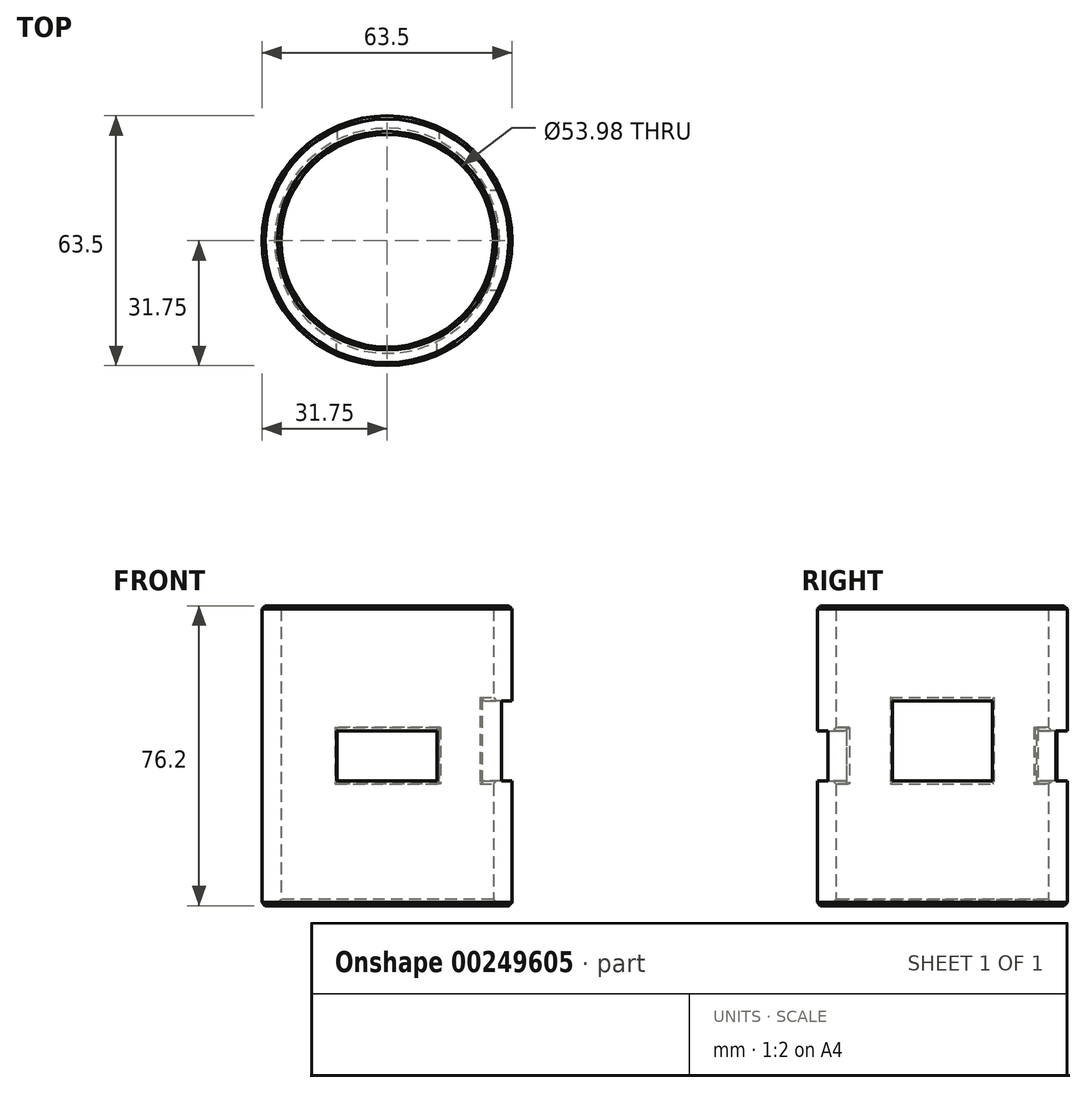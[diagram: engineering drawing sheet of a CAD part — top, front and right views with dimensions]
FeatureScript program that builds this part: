
annotation { "Feature Type Name" : "Feature", "Feature Type Description" : "" }
export const myFeature = defineFeature(function(context is Context, id is Id, definition is map)
    precondition{}
    {
        {
            var Q0;
            Q0=qCreatedBy(makeId("Top.planeOp"),FACE);
            var sketch = newSketch(context, id + "F0", { "sketchPlane" : qUnion([Q0])});
            skCircle(sketch, "E0", {"center": v(0, 0) * mm, "radius": 26.99 * mm});
            skCircle(sketch, "E1", {"center": v(0, 0) * mm, "radius": 31.75 * mm});
            skSolve(sketch);
        }
        {
            var Q0;
            Q0=makeQuery(id+"F0.imprint","IMPRINT",FACE,{"disambiguationData":[TD([[makeQuery(id+"F0.imprint","IMPRINT",EDGE,{"derivedFrom":sQuery(id+"F0.wireOp",EDGE,"E0")}),-1.0]])]});
            extrude(context, id + "F1", {"entities" : qUnion([Q0]), "depth" : 76.2 * mm});
        }
        {
            var Q0;
            Q0=qCreatedBy(makeId("Front.planeOp"),FACE);
            var sketch = newSketch(context, id + "F2", { "sketchPlane" : qUnion([Q0])});
            skLineSegment(sketch, "E2.bottom", {"start": v(13.22, 31.75) * mm, "end": v(-12.7, 31.75) * mm});
            skLineSegment(sketch, "E2.top", {"start": v(13.22, 44.45) * mm, "end": v(-12.7, 44.45) * mm});
            skLineSegment(sketch, "E2.left", {"start": v(13.22, 31.75) * mm, "end": v(13.22, 44.45) * mm});
            skLineSegment(sketch, "E2.right", {"start": v(-12.7, 31.75) * mm, "end": v(-12.7, 44.45) * mm});
            skSolve(sketch);
        }
        {
            var Q0;
            Q0 = qSketchRegion(id + "F2", true);
            extrude(context, id + "F3", {"entities" : qUnion([Q0]), "operationType" : NewBodyOperationType.REMOVE, "oppositeDirection" : true, "depth" : 76.2 * mm});
        }
        {
            var Q0;
            Q0=qCreatedBy(makeId("Front.planeOp"),FACE);
            var sketch = newSketch(context, id + "F4", { "sketchPlane" : qUnion([Q0])});
            skLineSegment(sketch, "E3.bottom", {"start": v(-12.77, 31.75) * mm, "end": v(12.7, 31.75) * mm});
            skLineSegment(sketch, "E3.top", {"start": v(-12.77, 44.45) * mm, "end": v(12.7, 44.45) * mm});
            skLineSegment(sketch, "E3.left", {"start": v(-12.77, 31.75) * mm, "end": v(-12.77, 44.45) * mm});
            skLineSegment(sketch, "E3.right", {"start": v(12.7, 31.75) * mm, "end": v(12.7, 44.45) * mm});
            skSolve(sketch);
        }
        {
            var Q0;
            Q0=makeQuery(id+"F4.imprint","IMPRINT",FACE,{"disambiguationData":[TD([[makeQuery(id+"F4.imprint","IMPRINT",EDGE,{"derivedFrom":sQuery(id+"F4.wireOp",EDGE,"E3.bottom")}),1.0]])]});
            extrude(context, id + "F5", {"entities" : qUnion([Q0]), "operationType" : NewBodyOperationType.REMOVE, "depth" : 76.2 * mm});
        }
        {
            var Q0;
            Q0=qCreatedBy(makeId("Right.planeOp"),FACE);
            var sketch = newSketch(context, id + "F6", { "sketchPlane" : qUnion([Q0])});
            skLineSegment(sketch, "E4.bottom", {"start": v(-12.7, 31.75) * mm, "end": v(12.7, 31.75) * mm});
            skLineSegment(sketch, "E4.top", {"start": v(-12.7, 52.07) * mm, "end": v(12.7, 52.07) * mm});
            skLineSegment(sketch, "E4.left", {"start": v(-12.7, 31.75) * mm, "end": v(-12.7, 52.07) * mm});
            skLineSegment(sketch, "E4.right", {"start": v(12.7, 31.75) * mm, "end": v(12.7, 52.07) * mm});
            skSolve(sketch);
        }
        {
            var Q0;
            Q0 = qSketchRegion(id + "F6", true);
            extrude(context, id + "F7", {"entities" : qUnion([Q0]), "operationType" : NewBodyOperationType.REMOVE, "depth" : 76.2 * mm});
        }
        {
            var Q0;
            Q0=makeQuery(id+"F7.boolean.opBoolean","INTERSECT",EDGE,{"derivedFrom":[makeQuery(id+"F1.opExtrude","SWEPT_FACE",FACE,{"disambiguationData":[OSD([sQuery(id+"F0.wireOp",EDGE,"E0")])]}),makeQuery(id+"F7.opExtrude","SWEPT_FACE",FACE,{"disambiguationData":[OSD([sQuery(id+"F6.wireOp",EDGE,"E4.bottom")])]})]});
            var Q1;
            Q1=makeQuery(id+"F7.boolean.opBoolean","INTERSECT",EDGE,{"derivedFrom":[makeQuery(id+"F1.opExtrude","SWEPT_FACE",FACE,{"disambiguationData":[OSD([sQuery(id+"F0.wireOp",EDGE,"E0")])]}),makeQuery(id+"F7.opExtrude","SWEPT_FACE",FACE,{"disambiguationData":[OSD([sQuery(id+"F6.wireOp",EDGE,"E4.right")])]})]});
            var Q2;
            Q2=makeQuery(id+"F7.boolean.opBoolean","INTERSECT",EDGE,{"derivedFrom":[makeQuery(id+"F1.opExtrude","SWEPT_FACE",FACE,{"disambiguationData":[OSD([sQuery(id+"F0.wireOp",EDGE,"E0")])]}),makeQuery(id+"F7.opExtrude","SWEPT_FACE",FACE,{"disambiguationData":[OSD([sQuery(id+"F6.wireOp",EDGE,"E4.top")])]})]});
            var Q3;
            Q3=makeQuery(id+"F7.boolean.opBoolean","INTERSECT",EDGE,{"derivedFrom":[makeQuery(id+"F1.opExtrude","SWEPT_FACE",FACE,{"disambiguationData":[OSD([sQuery(id+"F0.wireOp",EDGE,"E0")])]}),makeQuery(id+"F7.opExtrude","SWEPT_FACE",FACE,{"disambiguationData":[OSD([sQuery(id+"F6.wireOp",EDGE,"E4.left")])]})]});
            var Q4;
            Q4=makeQuery(id+"F3.boolean.opBoolean","INTERSECT",EDGE,{"derivedFrom":[makeQuery(id+"F1.opExtrude","SWEPT_FACE",FACE,{"disambiguationData":[OSD([sQuery(id+"F0.wireOp",EDGE,"E0")])]}),makeQuery(id+"F3.opExtrude","SWEPT_FACE",FACE,{"disambiguationData":[OSD([sQuery(id+"F2.wireOp",EDGE,"E2.left")])]})]});
            var Q5;
            Q5=makeQuery(id+"F3.boolean.opBoolean","INTERSECT",EDGE,{"derivedFrom":[makeQuery(id+"F1.opExtrude","SWEPT_FACE",FACE,{"disambiguationData":[OSD([sQuery(id+"F0.wireOp",EDGE,"E0")])]}),makeQuery(id+"F3.opExtrude","SWEPT_FACE",FACE,{"disambiguationData":[OSD([sQuery(id+"F2.wireOp",EDGE,"E2.bottom")])]})]});
            var Q6;
            Q6=makeQuery(id+"F3.boolean.opBoolean","INTERSECT",EDGE,{"derivedFrom":[makeQuery(id+"F1.opExtrude","SWEPT_FACE",FACE,{"disambiguationData":[OSD([sQuery(id+"F0.wireOp",EDGE,"E0")])]}),makeQuery(id+"F3.opExtrude","SWEPT_FACE",FACE,{"disambiguationData":[OSD([sQuery(id+"F2.wireOp",EDGE,"E2.top")])]})]});
            var Q7;
            Q7=makeQuery(id+"F3.boolean.opBoolean","INTERSECT",EDGE,{"derivedFrom":[makeQuery(id+"F1.opExtrude","SWEPT_FACE",FACE,{"disambiguationData":[OSD([sQuery(id+"F0.wireOp",EDGE,"E0")])]}),makeQuery(id+"F3.opExtrude","SWEPT_FACE",FACE,{"disambiguationData":[OSD([sQuery(id+"F2.wireOp",EDGE,"E2.right")])]})]});
            var Q8;
            Q8=makeQuery(id+"F5.boolean.opBoolean","INTERSECT",EDGE,{"derivedFrom":[makeQuery(id+"F1.opExtrude","SWEPT_FACE",FACE,{"disambiguationData":[OSD([sQuery(id+"F0.wireOp",EDGE,"E0")])]}),makeQuery(id+"F5.opExtrude","SWEPT_FACE",FACE,{"disambiguationData":[OSD([sQuery(id+"F4.wireOp",EDGE,"E3.right")])]})]});
            var Q9;
            Q9=makeQuery(id+"F5.boolean.opBoolean","INTERSECT",EDGE,{"derivedFrom":[makeQuery(id+"F1.opExtrude","SWEPT_FACE",FACE,{"disambiguationData":[OSD([sQuery(id+"F0.wireOp",EDGE,"E0")])]}),makeQuery(id+"F5.opExtrude","SWEPT_FACE",FACE,{"disambiguationData":[OSD([sQuery(id+"F4.wireOp",EDGE,"E3.left")])]})]});
            var Q10;
            Q10=makeQuery(id+"F5.boolean.opBoolean","INTERSECT",EDGE,{"derivedFrom":[makeQuery(id+"F1.opExtrude","SWEPT_FACE",FACE,{"disambiguationData":[OSD([sQuery(id+"F0.wireOp",EDGE,"E0")])]}),makeQuery(id+"F5.opExtrude","SWEPT_FACE",FACE,{"disambiguationData":[OSD([sQuery(id+"F4.wireOp",EDGE,"E3.bottom")])]})]});
            var Q11;
            Q11=makeQuery(id+"F5.boolean.opBoolean","INTERSECT",EDGE,{"derivedFrom":[makeQuery(id+"F1.opExtrude","SWEPT_FACE",FACE,{"disambiguationData":[OSD([sQuery(id+"F0.wireOp",EDGE,"E0")])]}),makeQuery(id+"F5.opExtrude","SWEPT_FACE",FACE,{"disambiguationData":[OSD([sQuery(id+"F4.wireOp",EDGE,"E3.top")])]})]});
            chamfer(context, id + "F8", {"entities" : qUnion([Q0, Q1, Q2, Q3, Q4, Q5, Q6, Q7, Q8, Q9, Q10, Q11]), "width" : 0.81 * mm, "tangentPropagation" : true});
        }
        {
            var Q0;
            Q0=makeQuery(id+"F1.opExtrude","CAP_EDGE",EDGE,{"disambiguationData":[OSD([sQuery(id+"F0.wireOp",EDGE,"E0")])],"isStart":false});
            var Q1;
            Q1=makeQuery(id+"F1.opExtrude","CAP_EDGE",EDGE,{"disambiguationData":[OSD([sQuery(id+"F0.wireOp",EDGE,"E1")])],"isStart":false});
            var Q2;
            Q2=makeQuery(id+"F1.opExtrude","CAP_EDGE",EDGE,{"disambiguationData":[OSD([sQuery(id+"F0.wireOp",EDGE,"E1")])],"isStart":true});
            chamfer(context, id + "F9", {"entities" : qUnion([Q0, Q1, Q2]), "width" : 0.81 * mm, "tangentPropagation" : true});
        }
        {
            var Q0;
            Q0=makeQuery(id+"F1.opExtrude","CAP_EDGE",EDGE,{"disambiguationData":[OSD([sQuery(id+"F0.wireOp",EDGE,"E0")])],"isStart":true});
            chamfer(context, id + "F10", {"entities" : qUnion([Q0]), "width" : 1.6 * mm, "tangentPropagation" : true});
        }
    });
